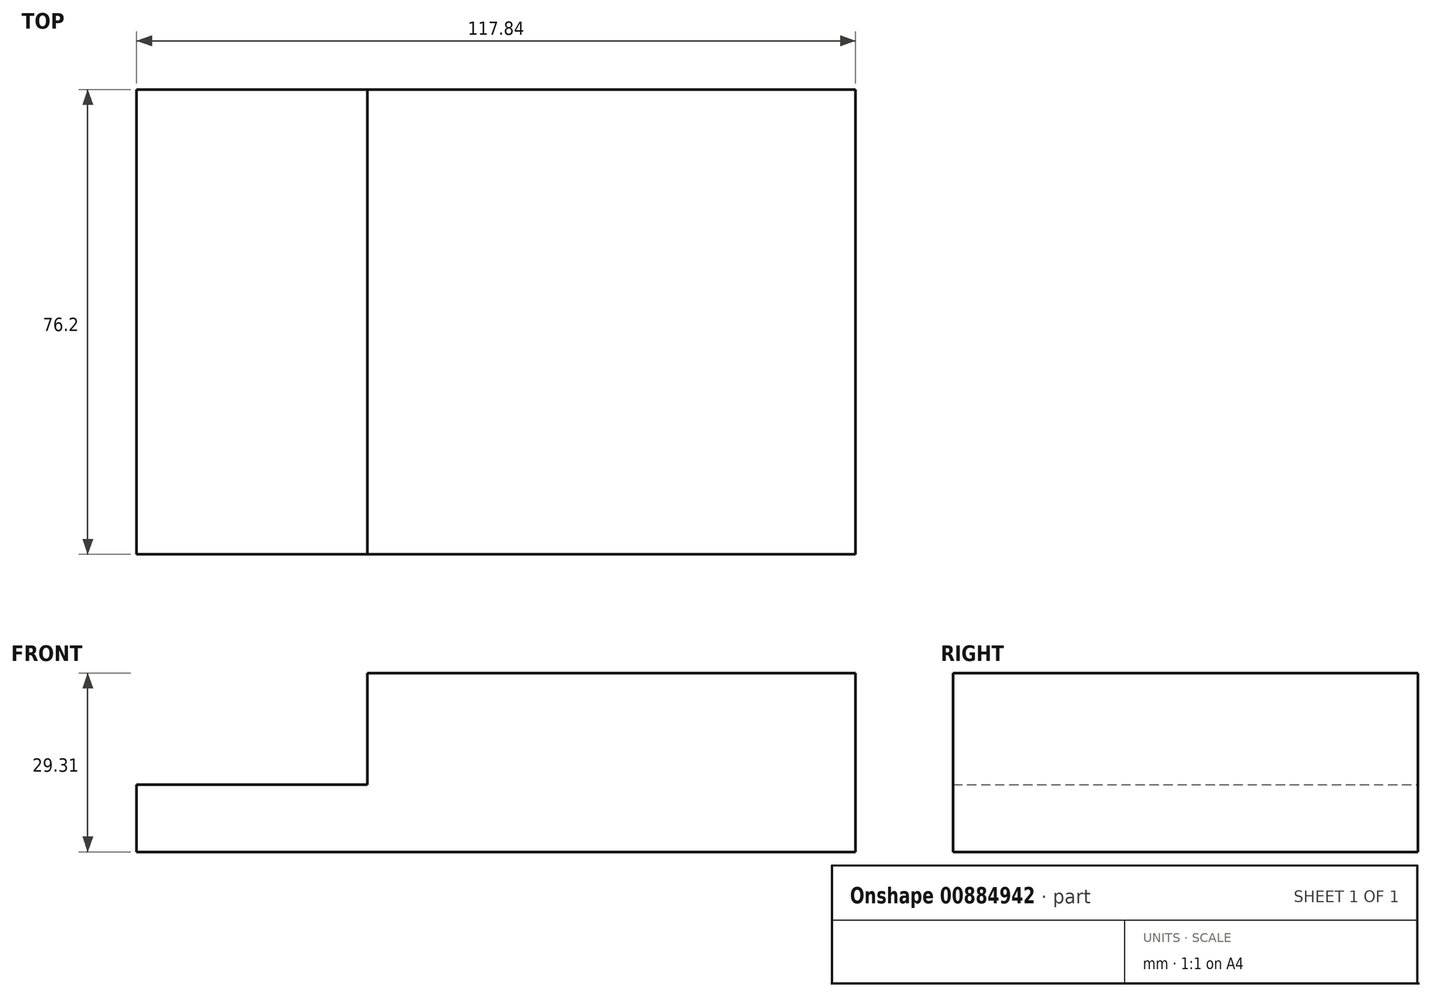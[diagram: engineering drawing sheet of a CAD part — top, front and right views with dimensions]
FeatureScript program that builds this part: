
annotation { "Feature Type Name" : "Feature", "Feature Type Description" : "" }
export const myFeature = defineFeature(function(context is Context, id is Id, definition is map)
    precondition{}
    {
        {
            var Q0;
            Q0=qCreatedBy(makeId("Front.planeOp"),FACE);
            var sketch = newSketch(context, id + "F0", { "sketchPlane" : qUnion([Q0])});
            skLineSegment(sketch, "E0.bottom", {"start": v(-27.45, 29.3) * mm, "end": v(52.56, 29.3) * mm});
            skLineSegment(sketch, "E0.top", {"start": v(-27.45, 0) * mm, "end": v(52.56, 0) * mm});
            skLineSegment(sketch, "E0.left", {"start": v(-27.45, 29.3) * mm, "end": v(-27.45, 11) * mm});
            skLineSegment(sketch, "E0.right", {"start": v(52.56, 29.3) * mm, "end": v(52.56, 0) * mm});
            skLineSegment(sketch, "E1.bottom", {"start": v(-65.28, 11) * mm, "end": v(-27.45, 11) * mm});
            skLineSegment(sketch, "E1.top", {"start": v(-65.28, 0) * mm, "end": v(-27.45, 0) * mm});
            skLineSegment(sketch, "E1.left", {"start": v(-65.28, 11) * mm, "end": v(-65.28, 0) * mm});
            skSolve(sketch);
        }
        {
            var Q0;
            Q0 = qSketchRegion(id + "F0", true);
            extrude(context, id + "F1", {"entities" : qUnion([Q0]), "flatOperationType" : FlatOperationType.REMOVE, "depth" : 76.2 * mm, "offsetDistance" : 25.4 * mm, "domain" : OperationDomain.MODEL});
        }
    });
